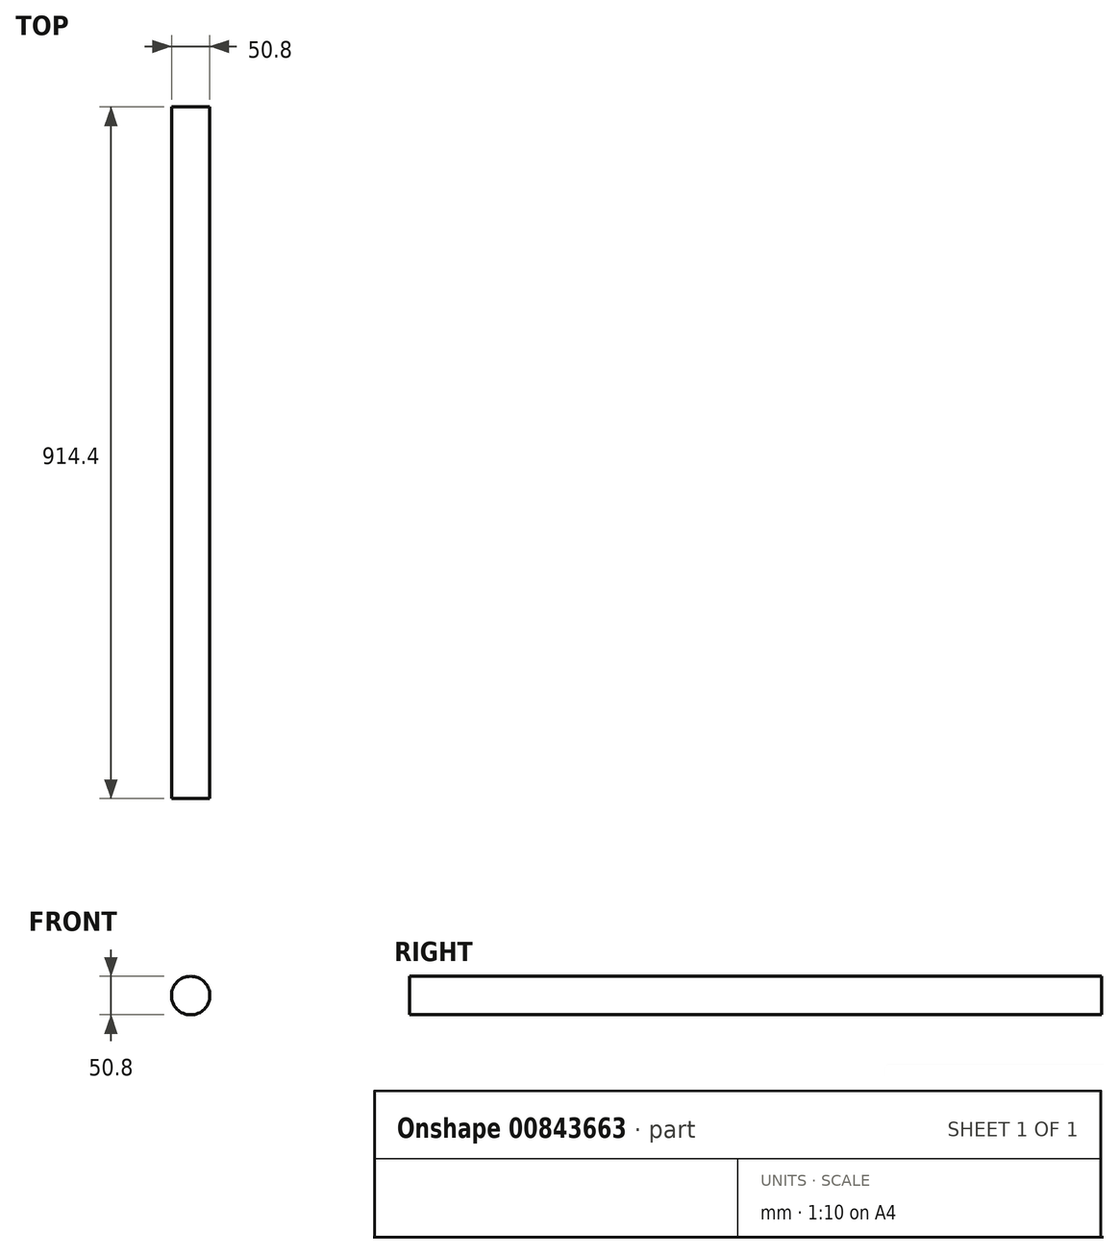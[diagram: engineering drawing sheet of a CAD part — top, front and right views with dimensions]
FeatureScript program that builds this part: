
annotation { "Feature Type Name" : "Feature", "Feature Type Description" : "" }
export const myFeature = defineFeature(function(context is Context, id is Id, definition is map)
    precondition{}
    {
        {
            var Q0;
            Q0=qCreatedBy(makeId("Front.planeOp"),FACE);
            var sketch = newSketch(context, id + "F0", { "sketchPlane" : qUnion([Q0])});
            skCircle(sketch, "E0", {"center": v(0, 0) * mm, "radius": 25.4 * mm});
            skSolve(sketch);
        }
        {
            var Q0;
            Q0 = qSketchRegion(id + "F0", true);
            extrude(context, id + "F1", {"entities" : qUnion([Q0]), "depth" : 914.4 * mm, "offsetDistance" : 25.4 * mm});
        }
    });
